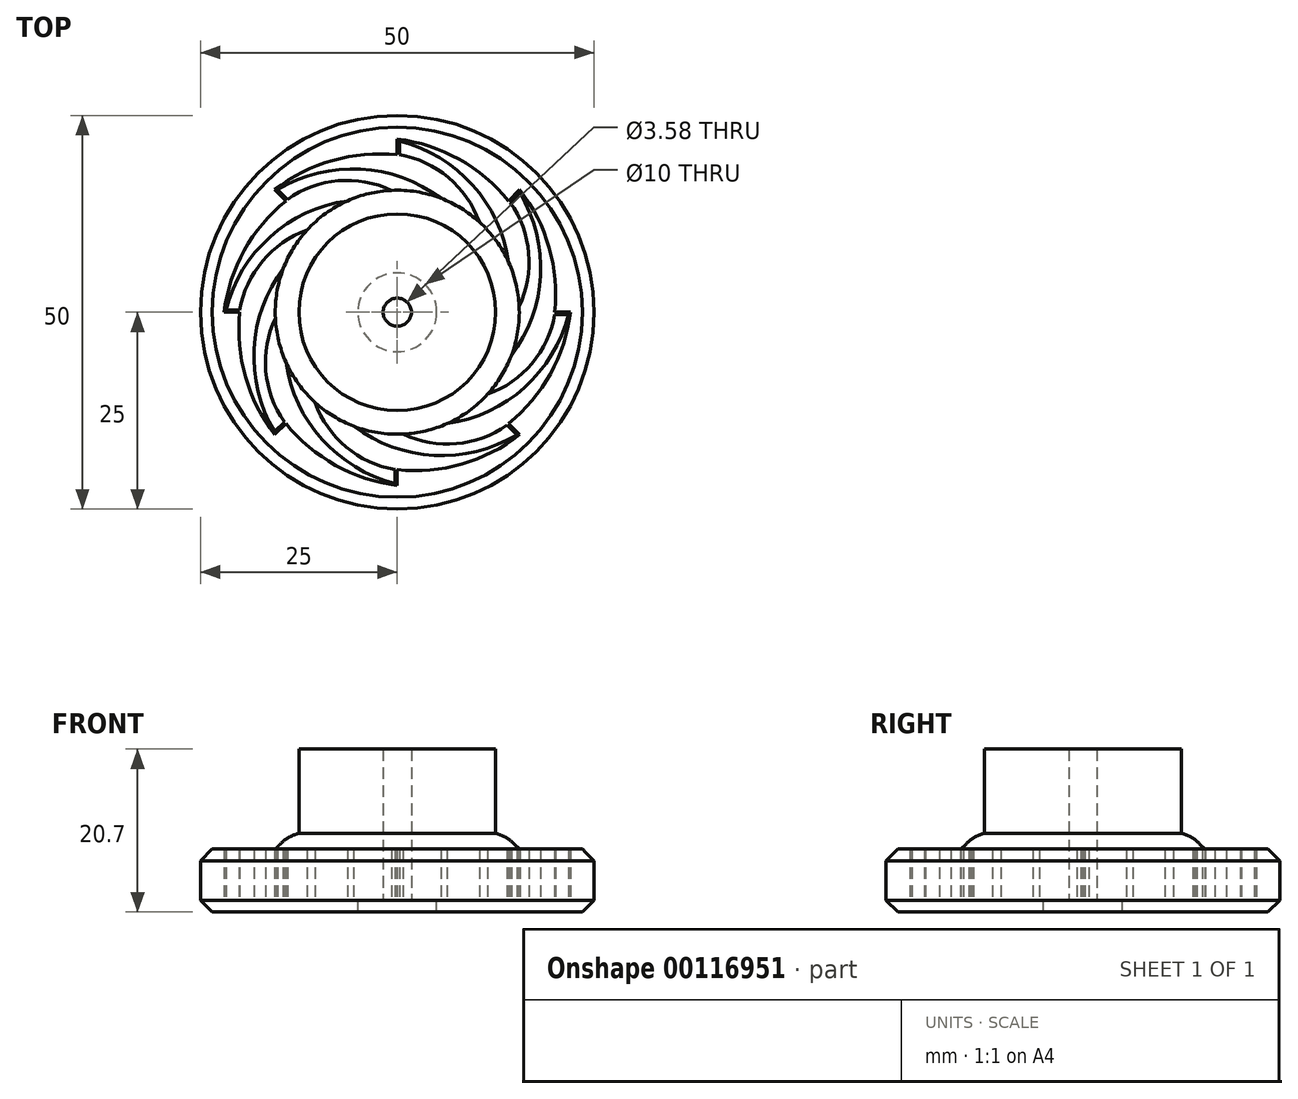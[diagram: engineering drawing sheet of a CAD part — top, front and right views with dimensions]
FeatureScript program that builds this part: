
annotation { "Feature Type Name" : "Feature", "Feature Type Description" : "" }
export const myFeature = defineFeature(function(context is Context, id is Id, definition is map)
    precondition{}
    {
        {
            var Q0;
            Q0=qCreatedBy(makeId("Top.planeOp"),FACE);
            var sketch = newSketch(context, id + "F0", { "sketchPlane" : qUnion([Q0])});
            skCircle(sketch, "E0", {"center": v(0, 0) * mm, "radius": 25 * mm});
            skCircle(sketch, "E1", {"center": v(0, 0) * mm, "radius": 1.8 * mm});
            skArc(sketch, "E2", {"start": v(-0.75, 15.48) * mm, "mid": v(-3.6, 15.08) * mm, "end": v(-6.33, 14.15) * mm});
            skLineSegment(sketch, "E3", {"start": v(0, 25) * mm, "end": v(0, -25) * mm, "construction": true});
            skLineSegment(sketch, "E4", {"start": v(-25, 0) * mm, "end": v(25, 0) * mm, "construction": true});
            skLineSegment(sketch, "E5", {"start": v(-17.68, 17.68) * mm, "end": v(17.68, -17.68) * mm, "construction": true});
            skLineSegment(sketch, "E6", {"start": v(17.68, 17.68) * mm, "end": v(-17.68, -17.68) * mm, "construction": true});
            skArc(sketch, "E7", {"start": v(0, 20) * mm, "mid": v(-8.2, 19.29) * mm, "end": v(-15.56, 15.56) * mm});
            skLineSegment(sketch, "E8", {"start": v(0, 22) * mm, "end": v(0, 20) * mm});
            skLineSegment(sketch, "E9", {"start": v(0.28, 20) * mm, "end": v(0.28, 21.75) * mm});
            skArc(sketch, "E10.1.0", {"start": v(-14.14, 14.14) * mm, "mid": v(-19.44, 7.83) * mm, "end": v(-22, 0) * mm});
            skLineSegment(sketch, "E10.1.1", {"start": v(-15.56, 15.56) * mm, "end": v(-14.14, 14.14) * mm});
            skArc(sketch, "E10.2.0", {"start": v(-20, 0) * mm, "mid": v(-19.29, -8.2) * mm, "end": v(-15.56, -15.56) * mm});
            skLineSegment(sketch, "E10.2.1", {"start": v(-22, 0) * mm, "end": v(-20, 0) * mm});
            skArc(sketch, "E10.3.0", {"start": v(-14.14, -14.14) * mm, "mid": v(-7.83, -19.44) * mm, "end": v(0, -22) * mm});
            skLineSegment(sketch, "E10.3.1", {"start": v(-15.56, -15.56) * mm, "end": v(-14.14, -14.14) * mm});
            skArc(sketch, "E10.4.0", {"start": v(0, -20) * mm, "mid": v(8.2, -19.29) * mm, "end": v(15.56, -15.56) * mm});
            skLineSegment(sketch, "E10.4.1", {"start": v(0, -22) * mm, "end": v(0, -20) * mm});
            skArc(sketch, "E10.5.0", {"start": v(14.14, -14.14) * mm, "mid": v(19.44, -7.83) * mm, "end": v(22, 0) * mm});
            skLineSegment(sketch, "E10.5.1", {"start": v(15.56, -15.56) * mm, "end": v(14.14, -14.14) * mm});
            skArc(sketch, "E10.6.0", {"start": v(20, 0) * mm, "mid": v(19.29, 8.2) * mm, "end": v(15.56, 15.56) * mm});
            skLineSegment(sketch, "E10.6.1", {"start": v(22, 0) * mm, "end": v(20, 0) * mm});
            skArc(sketch, "E10.7.0", {"start": v(14.14, 14.14) * mm, "mid": v(7.83, 19.44) * mm, "end": v(0, 22) * mm});
            skLineSegment(sketch, "E10.7.1", {"start": v(15.56, 15.56) * mm, "end": v(14.14, 14.14) * mm});
            skArc(sketch, "E11", {"start": v(14.15, 6.33) * mm, "mid": v(9.57, 16.16) * mm, "end": v(0.28, 21.75) * mm});
            skArc(sketch, "E12", {"start": v(10.42, 11.48) * mm, "mid": v(6.5, 17.12) * mm, "end": v(0.28, 20) * mm});
            skArc(sketch, "E13.1.0", {"start": v(-0.75, 15.48) * mm, "mid": v(-7.5, 16.7) * mm, "end": v(-13.94, 14.34) * mm});
            skArc(sketch, "E13.1.1", {"start": v(5.53, 14.48) * mm, "mid": v(-4.66, 18.2) * mm, "end": v(-15.18, 15.57) * mm});
            skLineSegment(sketch, "E13.1.2", {"start": v(-13.94, 14.34) * mm, "end": v(-15.18, 15.57) * mm});
            skArc(sketch, "E13.2.0", {"start": v(-11.48, 10.42) * mm, "mid": v(-17.12, 6.5) * mm, "end": v(-20, 0.28) * mm});
            skArc(sketch, "E13.2.1", {"start": v(-6.33, 14.15) * mm, "mid": v(-16.16, 9.57) * mm, "end": v(-21.75, 0.28) * mm});
            skLineSegment(sketch, "E13.2.2", {"start": v(-20, 0.28) * mm, "end": v(-21.75, 0.28) * mm});
            skArc(sketch, "E13.3.0", {"start": v(-15.48, -0.75) * mm, "mid": v(-16.7, -7.5) * mm, "end": v(-14.34, -13.94) * mm});
            skArc(sketch, "E13.3.1", {"start": v(-14.48, 5.53) * mm, "mid": v(-18.2, -4.66) * mm, "end": v(-15.57, -15.18) * mm});
            skLineSegment(sketch, "E13.3.2", {"start": v(-14.34, -13.94) * mm, "end": v(-15.57, -15.18) * mm});
            skArc(sketch, "E13.4.0", {"start": v(-10.42, -11.48) * mm, "mid": v(-6.5, -17.12) * mm, "end": v(-0.28, -20) * mm});
            skArc(sketch, "E13.4.1", {"start": v(-14.15, -6.33) * mm, "mid": v(-9.57, -16.16) * mm, "end": v(-0.28, -21.75) * mm});
            skLineSegment(sketch, "E13.4.2", {"start": v(-0.28, -20) * mm, "end": v(-0.28, -21.75) * mm});
            skArc(sketch, "E13.5.0", {"start": v(0.75, -15.48) * mm, "mid": v(7.5, -16.7) * mm, "end": v(13.94, -14.34) * mm});
            skArc(sketch, "E13.5.1", {"start": v(-5.53, -14.48) * mm, "mid": v(4.66, -18.2) * mm, "end": v(15.18, -15.57) * mm});
            skLineSegment(sketch, "E13.5.2", {"start": v(13.94, -14.34) * mm, "end": v(15.18, -15.57) * mm});
            skArc(sketch, "E13.6.0", {"start": v(11.48, -10.42) * mm, "mid": v(17.12, -6.5) * mm, "end": v(20, -0.28) * mm});
            skArc(sketch, "E13.6.1", {"start": v(6.33, -14.15) * mm, "mid": v(16.16, -9.57) * mm, "end": v(21.75, -0.28) * mm});
            skLineSegment(sketch, "E13.6.2", {"start": v(20, -0.28) * mm, "end": v(21.75, -0.28) * mm});
            skArc(sketch, "E13.7.0", {"start": v(15.48, 0.75) * mm, "mid": v(16.7, 7.5) * mm, "end": v(14.34, 13.94) * mm});
            skArc(sketch, "E13.7.1", {"start": v(14.48, -5.53) * mm, "mid": v(18.2, 4.66) * mm, "end": v(15.57, 15.18) * mm});
            skLineSegment(sketch, "E13.7.2", {"start": v(14.34, 13.94) * mm, "end": v(15.57, 15.18) * mm});
            skArc(sketch, "E14.trimOffspring", {"start": v(10.42, 11.48) * mm, "mid": v(8.11, 13.2) * mm, "end": v(5.53, 14.48) * mm});
            skArc(sketch, "E15.trimOffspring", {"start": v(15.48, 0.75) * mm, "mid": v(15.08, 3.6) * mm, "end": v(14.15, 6.33) * mm});
            skArc(sketch, "E16.trimOffspring", {"start": v(11.48, -10.42) * mm, "mid": v(13.2, -8.11) * mm, "end": v(14.48, -5.53) * mm});
            skArc(sketch, "E17.trimOffspring", {"start": v(-11.48, 10.42) * mm, "mid": v(-13.2, 8.11) * mm, "end": v(-14.48, 5.53) * mm});
            skArc(sketch, "E18.trimOffspring", {"start": v(-15.48, -0.75) * mm, "mid": v(-15.08, -3.6) * mm, "end": v(-14.15, -6.33) * mm});
            skArc(sketch, "E19.trimOffspring", {"start": v(-10.42, -11.48) * mm, "mid": v(-8.11, -13.2) * mm, "end": v(-5.53, -14.48) * mm});
            skArc(sketch, "E20.trimOffspring", {"start": v(0.75, -15.48) * mm, "mid": v(3.6, -15.08) * mm, "end": v(6.33, -14.15) * mm});
            skCircle(sketch, "E21", {"center": v(0, 0) * mm, "radius": 5 * mm, "construction": true});
            skSolve(sketch);
        }
        {
            var Q0;
            Q0=makeQuery(id+"F0.imprint","IMPRINT",FACE,{"disambiguationData":[TD([[makeQuery(id+"F0.imprint","IMPRINT",EDGE,{"derivedFrom":sQuery(id+"F0.wireOp",EDGE,"E0")}),1.0]])]});
            var Q1;
            Q1=makeQuery(id+"F0.imprint","IMPRINT",FACE,{"disambiguationData":[TD([[makeQuery(id+"F0.imprint","IMPRINT",EDGE,{"derivedFrom":sQuery(id+"F0.wireOp",EDGE,"E2")}),-1.0]])]});
            var Q2;
            Q2=makeQuery(id+"F0.imprint","IMPRINT",FACE,{"disambiguationData":[TD([[makeQuery(id+"F0.imprint","IMPRINT",EDGE,{"derivedFrom":sQuery(id+"F0.wireOp",EDGE,"E1")}),-1.0]])]});
            extrude(context, id + "F1", {"entities" : qUnion([Q0, Q1, Q2]), "oppositeDirection" : true, "depth" : 1.5 * mm});
        }
        {
            var Q0;
            Q0=makeQuery(id+"F0.imprint","IMPRINT",FACE,{"disambiguationData":[TD([[makeQuery(id+"F0.imprint","IMPRINT",EDGE,{"derivedFrom":sQuery(id+"F0.wireOp",EDGE,"E0")}),1.0]])]});
            extrude(context, id + "F2", {"entities" : qUnion([Q0]), "operationType" : NewBodyOperationType.ADD, "depth" : 6.5 * mm});
        }
        {
            var Q0;
            Q0=makeQuery(id+"F0.imprint","IMPRINT",FACE,{"disambiguationData":[TD([[makeQuery(id+"F0.imprint","IMPRINT",EDGE,{"derivedFrom":sQuery(id+"F0.wireOp",EDGE,"E1")}),-1.0]])]});
            extrude(context, id + "F3", {"entities" : qUnion([Q0]), "depth" : 6.5 * mm});
        }
        {
            var Q0;
            Q0=makeQuery(id+"F0.imprint","IMPRINT",FACE,{"disambiguationData":[TD([[makeQuery(id+"F0.imprint","IMPRINT",EDGE,{"derivedFrom":sQuery(id+"F0.wireOp",EDGE,"E1")}),-1.0]])]});
            var sketch = newSketch(context, id + "F4", { "sketchPlane" : qUnion([Q0])});
            skCircle(sketch, "E22.0", {"center": v(0, 0) * mm, "radius": 5 * mm});
            skSolve(sketch);
        }
        {
            var Q0;
            Q0=makeQuery(id+"F4.imprint","IMPRINT",FACE,{"disambiguationData":[TD([[makeQuery(id+"F4.imprint","IMPRINT",EDGE,{"derivedFrom":sQuery(id+"F4.wireOp",EDGE,"E22.0")}),1.0]])]});
            extrude(context, id + "F5", {"entities" : qUnion([Q0]), "operationType" : NewBodyOperationType.REMOVE, "endBound" : BoundingType.THROUGH_ALL, "oppositeDirection" : true, "depth" : 25.4 * mm});
        }
        {
            var Q0;
            Q0=makeQuery(id+"F3.opExtrude","CAP_FACE",FACE,{"disambiguationData":[OSD([sQuery(id+"F0.wireOp",EDGE,"E1"),sQuery(id+"F0.wireOp",EDGE,"E2"),sQuery(id+"F0.wireOp",EDGE,"E9"),sQuery(id+"F0.wireOp",EDGE,"E11"),sQuery(id+"F0.wireOp",EDGE,"E12"),sQuery(id+"F0.wireOp",EDGE,"E13.1.0"),sQuery(id+"F0.wireOp",EDGE,"E13.1.1"),sQuery(id+"F0.wireOp",EDGE,"E13.1.2"),sQuery(id+"F0.wireOp",EDGE,"E13.2.0"),sQuery(id+"F0.wireOp",EDGE,"E13.2.1"),sQuery(id+"F0.wireOp",EDGE,"E13.2.2"),sQuery(id+"F0.wireOp",EDGE,"E13.3.0"),sQuery(id+"F0.wireOp",EDGE,"E13.3.1"),sQuery(id+"F0.wireOp",EDGE,"E13.3.2"),sQuery(id+"F0.wireOp",EDGE,"E13.4.0"),sQuery(id+"F0.wireOp",EDGE,"E13.4.1"),sQuery(id+"F0.wireOp",EDGE,"E13.4.2"),sQuery(id+"F0.wireOp",EDGE,"E13.5.0"),sQuery(id+"F0.wireOp",EDGE,"E13.5.1"),sQuery(id+"F0.wireOp",EDGE,"E13.5.2"),sQuery(id+"F0.wireOp",EDGE,"E13.6.0"),sQuery(id+"F0.wireOp",EDGE,"E13.6.1"),sQuery(id+"F0.wireOp",EDGE,"E13.6.2"),sQuery(id+"F0.wireOp",EDGE,"E13.7.0"),sQuery(id+"F0.wireOp",EDGE,"E13.7.1"),sQuery(id+"F0.wireOp",EDGE,"E13.7.2"),sQuery(id+"F0.wireOp",EDGE,"E14.trimOffspring"),sQuery(id+"F0.wireOp",EDGE,"E15.trimOffspring"),sQuery(id+"F0.wireOp",EDGE,"E16.trimOffspring"),sQuery(id+"F0.wireOp",EDGE,"E17.trimOffspring"),sQuery(id+"F0.wireOp",EDGE,"E18.trimOffspring"),sQuery(id+"F0.wireOp",EDGE,"E19.trimOffspring"),sQuery(id+"F0.wireOp",EDGE,"E20.trimOffspring")])],"isStart":false});
            var sketch = newSketch(context, id + "F6", { "sketchPlane" : qUnion([Q0])});
            skArc(sketch, "E23.0", {"start": v(-11.48, 10.42) * mm, "mid": v(-13.2, 8.11) * mm, "end": v(-14.48, 5.53) * mm, "construction": true});
            skCircle(sketch, "E24", {"center": v(0, 0) * mm, "radius": 15.5 * mm});
            skCircle(sketch, "E25", {"center": v(0, 0) * mm, "radius": 12.5 * mm});
            skSolve(sketch);
        }
        {
            var Q0;
            Q0=makeQuery(id+"F6.imprint","IMPRINT",FACE,{"disambiguationData":[TD([[makeQuery(id+"F6.imprint","IMPRINT",EDGE,{"derivedFrom":sQuery(id+"F6.wireOp",EDGE,"E25")}),1.0]])]});
            extrude(context, id + "F7", {"entities" : qUnion([Q0]), "operationType" : NewBodyOperationType.ADD, "depth" : 12.7 * mm});
        }
        {
            var Q0;
            Q0=makeQuery(id+"F6.imprint","IMPRINT",FACE,{"disambiguationData":[TD([[makeQuery(id+"F6.imprint","IMPRINT",EDGE,{"derivedFrom":sQuery(id+"F6.wireOp",EDGE,"E25")}),-1.0]])]});
            extrude(context, id + "F8", {"entities" : qUnion([Q0]), "operationType" : NewBodyOperationType.ADD, "depth" : 2 * mm});
        }
        {
            var Q0;
            Q0=makeQuery(id+"F8.opExtrude","CAP_EDGE",EDGE,{"disambiguationData":[OSD([sQuery(id+"F6.wireOp",EDGE,"E24")])],"isStart":false});
            chamfer(context, id + "F9", {"entities" : qUnion([Q0]), "width" : 2 * mm, "tangentPropagation" : true});
        }
        {
            var Q0;
            {var subQ0=sQuery(id+"F6.wireOp",EDGE,"E24");Q0=makeQuery(id+"F9.opChamfer","BLEND_EDGE",EDGE,{"blendedFrom":[makeQuery(id+"F8.opExtrude","CAP_EDGE",EDGE,{"disambiguationData":[OSD([subQ0])],"isStart":false}),makeQuery(id+"F8.opExtrude","CAP_FACE",FACE,{"disambiguationData":[OSD([subQ0,sQuery(id+"F6.wireOp",EDGE,"E25")])],"isStart":false})],"blendedInto":[makeQuery(id+"F8.opExtrude","CAP_FACE",FACE,{"disambiguationData":[OSD([subQ0,sQuery(id+"F6.wireOp",EDGE,"E25")])],"isStart":false})]});}
            fillet(context, id + "F10", {"entities" : qUnion([Q0]), "radius" : 5 * mm, "tangentPropagation" : true, "allowEdgeOverflow" : false});
        }
        {
            var Q0;
            Q0=makeQuery(id+"F2.opExtrude","CAP_EDGE",EDGE,{"disambiguationData":[OSD([sQuery(id+"F0.wireOp",EDGE,"E0")])],"isStart":false});
            var Q1;
            Q1=makeQuery(id+"F1.opExtrude","CAP_EDGE",EDGE,{"disambiguationData":[OSD([sQuery(id+"F0.wireOp",EDGE,"E0")])],"isStart":false});
            chamfer(context, id + "F11", {"entities" : qUnion([Q0, Q1]), "width" : 1.5 * mm, "tangentPropagation" : true});
        }
    });
